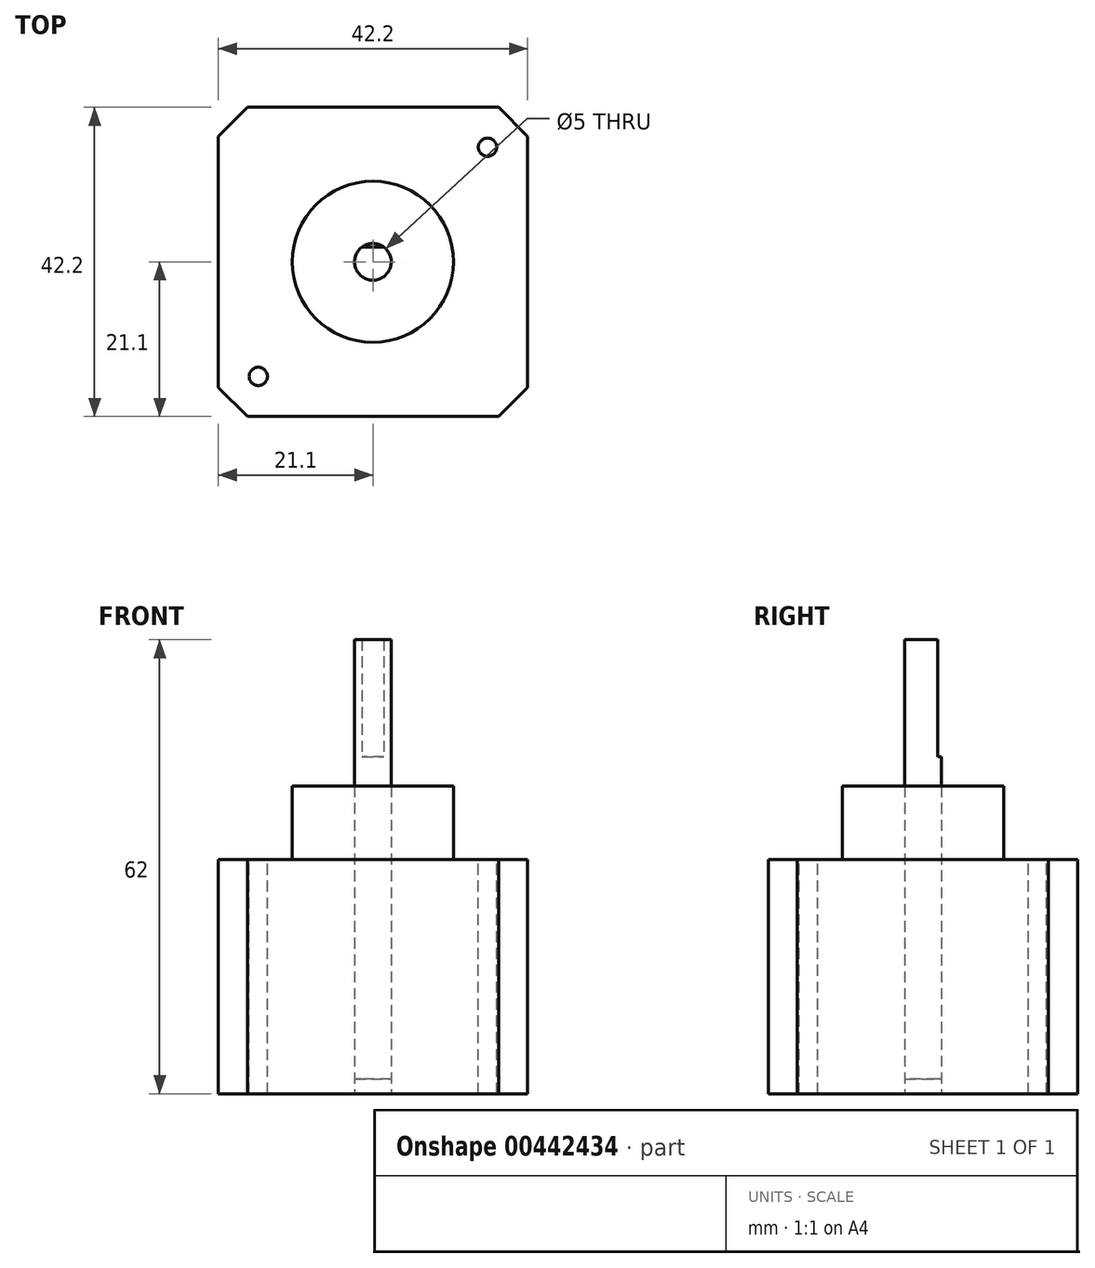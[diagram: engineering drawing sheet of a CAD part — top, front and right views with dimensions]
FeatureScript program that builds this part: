
annotation { "Feature Type Name" : "Feature", "Feature Type Description" : "" }
export const myFeature = defineFeature(function(context is Context, id is Id, definition is map)
    precondition{}
    {
        {
            var Q0;
            Q0=qCreatedBy(makeId("Top.planeOp"),FACE);
            var sketch = newSketch(context, id + "F0", { "sketchPlane" : qUnion([Q0])});
            skLineSegment(sketch, "E0.bottom", {"start": v(-21.1, 21.1) * mm, "end": v(21.1, 21.1) * mm});
            skLineSegment(sketch, "E0.top", {"start": v(-21.1, -21.1) * mm, "end": v(21.1, -21.1) * mm});
            skLineSegment(sketch, "E0.left", {"start": v(-21.1, 21.1) * mm, "end": v(-21.1, -21.1) * mm});
            skLineSegment(sketch, "E0.right", {"start": v(21.1, 21.1) * mm, "end": v(21.1, -21.1) * mm});
            skCircle(sketch, "E1", {"center": v(0, 0) * mm, "radius": 11 * mm});
            skCircle(sketch, "E2", {"center": v(0, 0) * mm, "radius": 2.5 * mm});
            skLineSegment(sketch, "E3", {"start": v(0, 21.1) * mm, "end": v(0, 0) * mm, "construction": true});
            skLineSegment(sketch, "E4", {"start": v(21.1, 0) * mm, "end": v(0, 0) * mm, "construction": true});
            skCircle(sketch, "E5", {"center": v(-15.65, 15.65) * mm, "radius": 1.25 * mm});
            skCircle(sketch, "E6.MirrorC", {"center": v(15.65, 15.65) * mm, "radius": 1.25 * mm});
            skCircle(sketch, "E7.MirrorC", {"center": v(-15.65, -15.65) * mm, "radius": 1.25 * mm});
            skCircle(sketch, "E8.MirrorC", {"center": v(15.65, -15.65) * mm, "radius": 1.25 * mm});
            skLineSegment(sketch, "E9", {"start": v(-17.14, 21.1) * mm, "end": v(-21.1, 17.14) * mm});
            skLineSegment(sketch, "E10.MirrorCS", {"start": v(17.14, 21.1) * mm, "end": v(21.1, 17.14) * mm});
            skLineSegment(sketch, "E11.MirrorCS", {"start": v(17.14, -21.1) * mm, "end": v(21.1, -17.14) * mm});
            skLineSegment(sketch, "E12.MirrorCS", {"start": v(-17.14, -21.1) * mm, "end": v(-21.1, -17.14) * mm});
            skLineSegment(sketch, "E13", {"start": v(-1.5, 2) * mm, "end": v(1.5, 2) * mm});
            skSolve(sketch);
        }
        {
            var Q0;
            Q0=makeQuery(id+"F0.imprint","IMPRINT",FACE,{"disambiguationData":[TD([[makeQuery(id+"F0.imprint","IMPRINT",EDGE,{"derivedFrom":sQuery(id+"F0.wireOp",EDGE,"E1")}),-1.0]])]});
            var Q1;
            Q1=makeQuery(id+"F0.imprint","IMPRINT",FACE,{"disambiguationData":[TD([[makeQuery(id+"F0.imprint","IMPRINT",EDGE,{"derivedFrom":sQuery(id+"F0.wireOp",EDGE,"E1")}),1.0]])]});
            var Q2;
            Q2=makeQuery(id+"F0.imprint","IMPRINT",FACE,{"disambiguationData":[TD([[makeQuery(id+"F0.imprint","IMPRINT",EDGE,{"derivedFrom":sQuery(id+"F0.wireOp",EDGE,"E2")}),1.0]])]});
            var Q3;
            Q3=makeQuery(id+"F0.imprint","IMPRINT",FACE,{"disambiguationData":[TD([[makeQuery(id+"F0.imprint","IMPRINT",EDGE,{"derivedFrom":sQuery(id+"F0.wireOp",EDGE,"E5")}),1.0]])]});
            var Q4;
            Q4=makeQuery(id+"F0.imprint","IMPRINT",FACE,{"disambiguationData":[TD([[makeQuery(id+"F0.imprint","IMPRINT",EDGE,{"derivedFrom":sQuery(id+"F0.wireOp",EDGE,"E6.MirrorC")}),-1.0]])]});
            var Q5;
            Q5=makeQuery(id+"F0.imprint","IMPRINT",FACE,{"disambiguationData":[TD([[makeQuery(id+"F0.imprint","IMPRINT",EDGE,{"derivedFrom":sQuery(id+"F0.wireOp",EDGE,"E8.MirrorC")}),1.0]])]});
            var Q6;
            Q6=makeQuery(id+"F0.imprint","IMPRINT",FACE,{"disambiguationData":[TD([[makeQuery(id+"F0.imprint","IMPRINT",EDGE,{"derivedFrom":sQuery(id+"F0.wireOp",EDGE,"E7.MirrorC")}),-1.0]])]});
            extrude(context, id + "F1", {"entities" : qUnion([Q0, Q1, Q2, Q3, Q4, Q5, Q6]), "oppositeDirection" : true, "depth" : 40 * mm});
        }
        {
            var Q0;
            Q0=makeQuery(id+"F0.imprint","IMPRINT",FACE,{"disambiguationData":[TD([[makeQuery(id+"F0.imprint","IMPRINT",EDGE,{"derivedFrom":sQuery(id+"F0.wireOp",EDGE,"E1")}),1.0]])]});
            extrude(context, id + "F2", {"entities" : qUnion([Q0]), "operationType" : NewBodyOperationType.ADD, "depth" : 2 * mm});
        }
        {
            var Q0;
            Q0=makeQuery(id+"F0.imprint","IMPRINT",FACE,{"disambiguationData":[TD([[makeQuery(id+"F0.imprint","IMPRINT",EDGE,{"derivedFrom":sQuery(id+"F0.wireOp",EDGE,"E2")}),1.0]])]});
            extrude(context, id + "F3", {"entities" : qUnion([Q0]), "operationType" : NewBodyOperationType.REMOVE, "endBound" : BoundingType.THROUGH_ALL, "oppositeDirection" : true, "depth" : 25 * mm});
        }
        {
            var Q0;
            Q0=makeQuery(id+"F0.imprint","IMPRINT",FACE,{"disambiguationData":[TD([[makeQuery(id+"F0.imprint","IMPRINT",EDGE,{"derivedFrom":sQuery(id+"F0.wireOp",EDGE,"E7.MirrorC")}),-1.0]])]});
            var Q1;
            Q1=makeQuery(id+"F0.imprint","IMPRINT",FACE,{"disambiguationData":[TD([[makeQuery(id+"F0.imprint","IMPRINT",EDGE,{"derivedFrom":sQuery(id+"F0.wireOp",EDGE,"E8.MirrorC")}),1.0]])]});
            var Q2;
            Q2=makeQuery(id+"F0.imprint","IMPRINT",FACE,{"disambiguationData":[TD([[makeQuery(id+"F0.imprint","IMPRINT",EDGE,{"derivedFrom":sQuery(id+"F0.wireOp",EDGE,"E6.MirrorC")}),-1.0]])]});
            var Q3;
            Q3=makeQuery(id+"F0.imprint","IMPRINT",FACE,{"disambiguationData":[TD([[makeQuery(id+"F0.imprint","IMPRINT",EDGE,{"derivedFrom":sQuery(id+"F0.wireOp",EDGE,"E5")}),1.0]])]});
            extrude(context, id + "F4", {"entities" : qUnion([Q0, Q1, Q2, Q3]), "operationType" : NewBodyOperationType.REMOVE, "oppositeDirection" : true, "depth" : 8 * mm});
        }
        {
            var Q0;
            Q0=makeQuery(id+"F0.imprint","IMPRINT",FACE,{"disambiguationData":[TD([[makeQuery(id+"F0.imprint","IMPRINT",EDGE,{"derivedFrom":sQuery(id+"F0.wireOp",EDGE,"E2")}),1.0]])]});
            extrude(context, id + "F5", {"entities" : qUnion([Q0]), "depth" : 22 * mm, "hasSecondDirection" : true, "secondDirectionOppositeDirection" : true, "secondDirectionDepth" : 38 * mm});
        }
        {
            var Q0;
            {var subQ0=sQuery(id+"F0.wireOp",EDGE,"E13");Q0=makeQuery(id+"F0.imprint","IMPRINT",FACE,{"disambiguationData":[TD([[makeQuery(id+"F0.imprint","IMPRINT",EDGE,{"derivedFrom":subQ0}),1.0]])]});}
            extrude(context, id + "F6", {"entities" : qUnion([Q0]), "operationType" : NewBodyOperationType.REMOVE, "depth" : 22 * mm, "hasSecondDirection" : true, "secondDirectionOppositeDirection" : false, "secondDirectionDepth" : 6 * mm});
        }
    });
